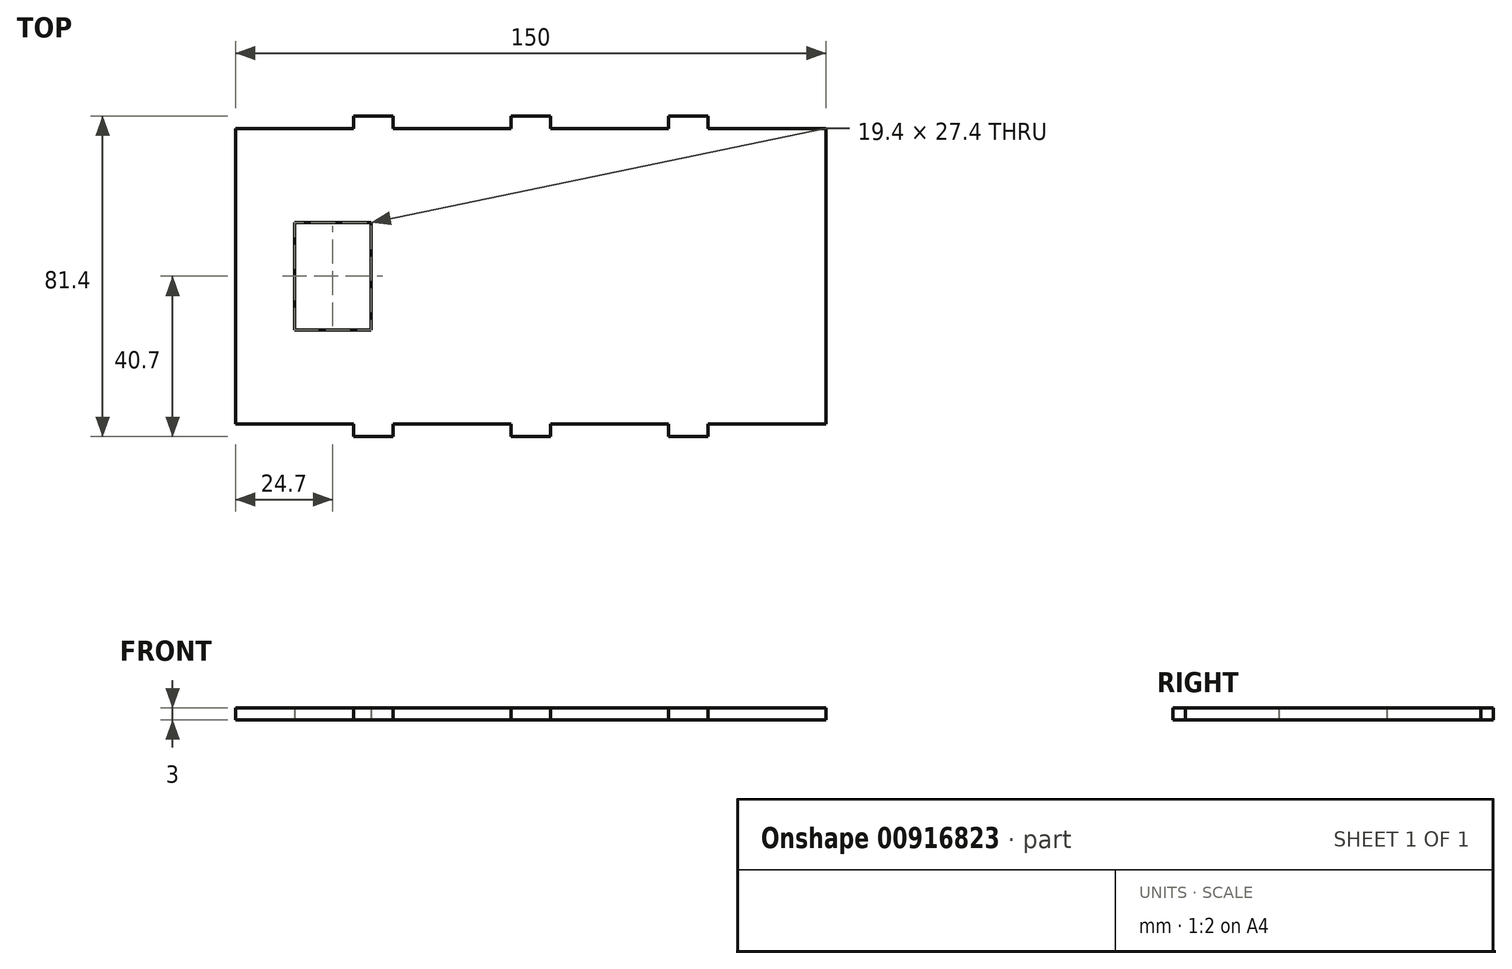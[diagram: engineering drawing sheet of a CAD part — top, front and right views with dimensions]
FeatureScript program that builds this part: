
annotation { "Feature Type Name" : "Feature", "Feature Type Description" : "" }
export const myFeature = defineFeature(function(context is Context, id is Id, definition is map)
    precondition{}
    {
        {
            var Q0;
            Q0=qCreatedBy(makeId("Top.planeOp"),FACE);
            var sketch = newSketch(context, id + "F0", { "sketchPlane" : qUnion([Q0])});
            skLineSegment(sketch, "E0.bottom", {"start": v(-75, 37.5) * mm, "end": v(-45, 37.5) * mm});
            skLineSegment(sketch, "E0.top", {"start": v(-75, -37.5) * mm, "end": v(-45, -37.5) * mm});
            skLineSegment(sketch, "E0.left", {"start": v(-75, 37.5) * mm, "end": v(-75, -37.5) * mm});
            skLineSegment(sketch, "E0.right", {"start": v(75, 37.5) * mm, "end": v(75, -37.5) * mm});
            skLineSegment(sketch, "E1", {"start": v(0, 37.5) * mm, "end": v(0, -37.5) * mm, "construction": true});
            skLineSegment(sketch, "E2", {"start": v(-75, 0) * mm, "end": v(75, 0) * mm, "construction": true});
            skLineSegment(sketch, "E3.top", {"start": v(-45, 40.7) * mm, "end": v(-35, 40.7) * mm});
            skLineSegment(sketch, "E3.left", {"start": v(-45, 37.5) * mm, "end": v(-45, 40.7) * mm});
            skLineSegment(sketch, "E3.right", {"start": v(-35, 37.5) * mm, "end": v(-35, 40.7) * mm});
            skLineSegment(sketch, "E4.MirrorCS", {"start": v(35, 37.5) * mm, "end": v(35, 40.7) * mm});
            skLineSegment(sketch, "E5.MirrorCS", {"start": v(45, 37.5) * mm, "end": v(45, 40.7) * mm});
            skLineSegment(sketch, "E6.MirrorCS", {"start": v(45, 40.7) * mm, "end": v(35, 40.7) * mm});
            skLineSegment(sketch, "E7.trimOffspring", {"start": v(-35, 37.5) * mm, "end": v(-5, 37.5) * mm});
            skLineSegment(sketch, "E8.trimOffspring", {"start": v(5, 37.5) * mm, "end": v(35, 37.5) * mm});
            skLineSegment(sketch, "E9.trimOffspring", {"start": v(45, 37.5) * mm, "end": v(75, 37.5) * mm});
            skLineSegment(sketch, "E10.MirrorCS", {"start": v(-45, -37.5) * mm, "end": v(-45, -40.7) * mm});
            skLineSegment(sketch, "E11.MirrorCS", {"start": v(35, -37.5) * mm, "end": v(35, -40.7) * mm});
            skLineSegment(sketch, "E12.MirrorCS", {"start": v(45, -37.5) * mm, "end": v(45, -40.7) * mm});
            skLineSegment(sketch, "E13.MirrorCS", {"start": v(-35, -37.5) * mm, "end": v(-35, -40.7) * mm});
            skLineSegment(sketch, "E14.MirrorCS", {"start": v(-45, -40.7) * mm, "end": v(-35, -40.7) * mm});
            skLineSegment(sketch, "E15.MirrorCS", {"start": v(45, -40.7) * mm, "end": v(35, -40.7) * mm});
            skLineSegment(sketch, "E16.MirrorCS", {"start": v(-35, -37.5) * mm, "end": v(-5, -37.5) * mm});
            skLineSegment(sketch, "E17.MirrorCS", {"start": v(5, -37.5) * mm, "end": v(35, -37.5) * mm});
            skLineSegment(sketch, "E18.trimOffspring", {"start": v(45, -37.5) * mm, "end": v(75, -37.5) * mm});
            skLineSegment(sketch, "E19.top", {"start": v(-5, -40.7) * mm, "end": v(5, -40.7) * mm});
            skLineSegment(sketch, "E19.left", {"start": v(-5, -37.5) * mm, "end": v(-5, -40.7) * mm});
            skLineSegment(sketch, "E19.right", {"start": v(5, -37.5) * mm, "end": v(5, -40.7) * mm});
            skLineSegment(sketch, "E20.MirrorCS", {"start": v(5, 37.5) * mm, "end": v(5, 40.7) * mm});
            skLineSegment(sketch, "E21.MirrorCS", {"start": v(-5, 37.5) * mm, "end": v(-5, 40.7) * mm});
            skLineSegment(sketch, "E22.MirrorCS", {"start": v(-5, 40.7) * mm, "end": v(5, 40.7) * mm});
            skLineSegment(sketch, "E23.bottom", {"start": v(-60, 13.7) * mm, "end": v(-40.6, 13.7) * mm});
            skLineSegment(sketch, "E23.top", {"start": v(-60, -13.7) * mm, "end": v(-40.6, -13.7) * mm});
            skLineSegment(sketch, "E23.left", {"start": v(-60, 13.7) * mm, "end": v(-60, -13.7) * mm});
            skLineSegment(sketch, "E23.right", {"start": v(-40.6, 13.7) * mm, "end": v(-40.6, -13.7) * mm});
            skSolve(sketch);
        }
        {
            var Q0;
            Q0=qSketchRegion(id+"F0",true);
            extrude(context, id + "F1", {"entities" : qUnion([Q0]), "depth" : 3 * mm, "offsetDistance" : 25 * mm});
        }
    });
